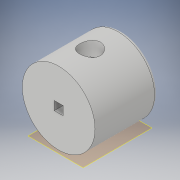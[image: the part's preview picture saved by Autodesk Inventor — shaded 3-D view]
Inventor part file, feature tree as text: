
AUTODESK INVENTOR PART (.ipt)
format: ipt  version: 2017 (Build 210142000, 142)  size: 146,944 bytes
history: native  units: in
note: dims shown in document units (in); Inventor stores cm internally (conversion verified against a paired STEP export)
features: sketch x4, extrude x2, plane x2, hole x2, chamfer x1, fillet x1
ambient origin geometry x8: Origin, YZ Plane, XZ Plane, XY Plane, X Axis, Y Axis, Z Axis, Center Point
bodies: Solid1 (feature_tree)
feature tree (12):
  extrude  "Extrusion1"  Depth=1.0in TaperAngle=0.0deg
  plane  "Work Plane2"
  sketch  "Sketch2"  dims[d3=0.5in d4=0.0in]
  sketch  "Sketch3"  dims[d5=0.5in d6=0.0in]
  hole  "Hole1"  [1 undecoded]
  hole  "Hole2"  [1 undecoded]
  extrude  "Extrusion2"  Depth=0.05in
  chamfer  "Chamfer1"  Distance=0.14in
  fillet  "Fillet1"  Radius=1.0in
  sketch  "Sketch1"  dims[d0=1.16in d1=1.0in d2=0.0in]
  plane  "Work Plane1"
  sketch  "Sketch4"  dims[d7=0.33in d8=0.75in d9=0.375in d10=0.25in d11=0.5635in d12=0.24in d13=60.0deg d14=0.33in d15=0.75in d16=0.375in d17=0.25in d18=0.5635in d19=0.24in d20=60.0deg d21=0.14in d22=0.14in d23=1.0in d24=0.0in d25=0.02in d26=0.125in d27=45.0deg d28=0.05in]
note: 2 required parameter values undecoded (feature->parameter linkage not recoverable at this tier; creation-order binding heuristic only, values carry confidence <= 0.55)
